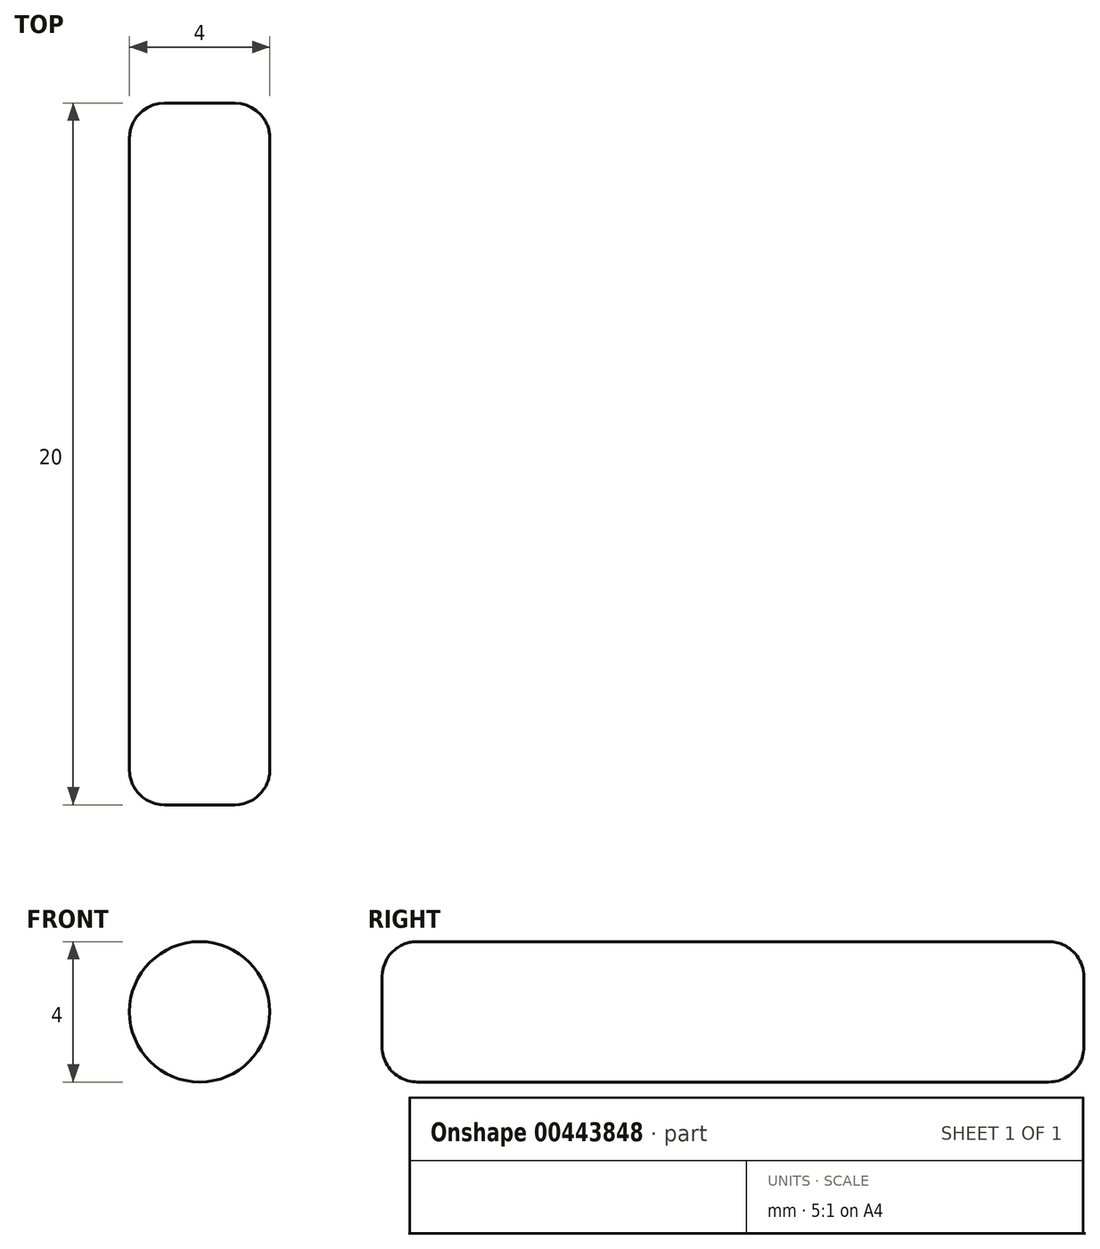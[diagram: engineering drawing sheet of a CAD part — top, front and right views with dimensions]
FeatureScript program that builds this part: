
annotation { "Feature Type Name" : "Feature", "Feature Type Description" : "" }
export const myFeature = defineFeature(function(context is Context, id is Id, definition is map)
    precondition{}
    {
        {
            var Q0;
            Q0=qCreatedBy(makeId("Front.planeOp"),FACE);
            var sketch = newSketch(context, id + "F0", { "sketchPlane" : qUnion([Q0])});
            skCircle(sketch, "E0", {"center": v(0, 0) * mm, "radius": 2 * mm});
            skSolve(sketch);
        }
        {
            var Q0;
            Q0 = qSketchRegion(id + "F0", true);
            extrude(context, id + "F1", {"entities" : qUnion([Q0]), "endBound" : BoundingType.SYMMETRIC, "depth" : 20 * mm});
        }
        {
            var Q0;
            Q0=makeQuery(id+"F1.opExtrude","CAP_FACE",FACE,{"disambiguationData":[OSD([sQuery(id+"F0.wireOp",EDGE,"E0")])],"isStart":false});
            var Q1;
            Q1=makeQuery(id+"F1.opExtrude","CAP_EDGE",EDGE,{"disambiguationData":[OSD([sQuery(id+"F0.wireOp",EDGE,"E0")])],"isStart":true});
            var Q2;
            Q2=makeQuery(id+"F1.opExtrude","SWEPT_FACE",FACE,{"disambiguationData":[OSD([sQuery(id+"F0.wireOp",EDGE,"E0")])]});
            fillet(context, id + "F2", {"entities" : qUnion([Q0, Q1, Q2]), "radius" : 1 * mm, "tangentPropagation" : true, "allowEdgeOverflow" : false});
        }
    });
